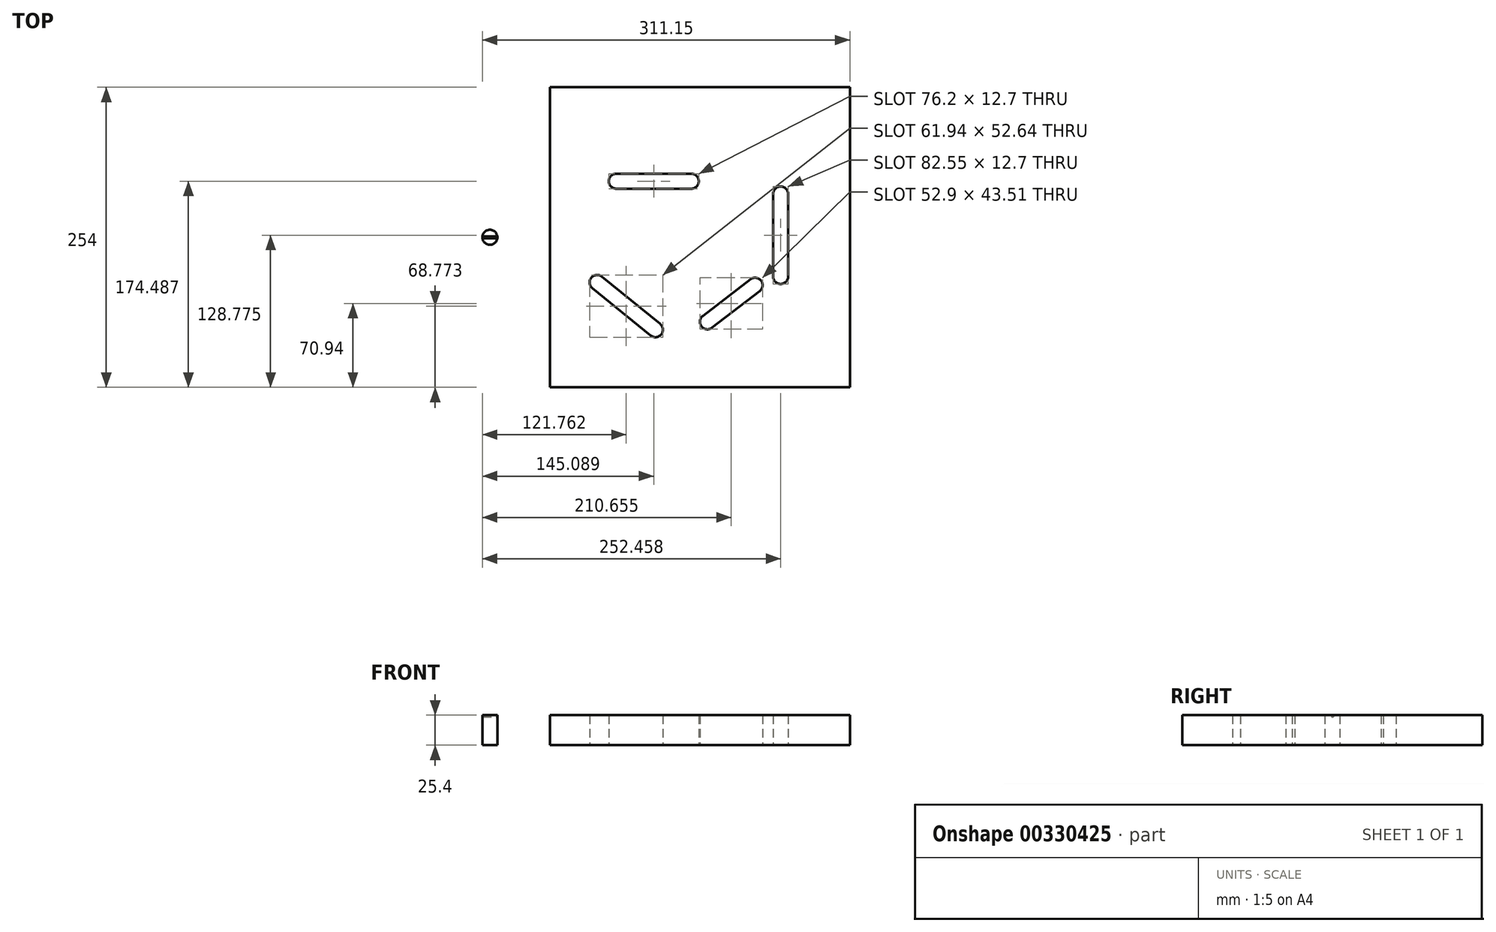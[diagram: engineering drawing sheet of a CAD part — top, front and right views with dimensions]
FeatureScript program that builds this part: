
annotation { "Feature Type Name" : "Feature", "Feature Type Description" : "" }
export const myFeature = defineFeature(function(context is Context, id is Id, definition is map)
    precondition{}
    {
        {
            var Q0;
            Q0=qCreatedBy(makeId("Top.planeOp"),FACE);
            var sketch = newSketch(context, id + "F0", { "sketchPlane" : qUnion([Q0])});
            skLineSegment(sketch, "E0.bottom", {"start": v(127, -127) * mm, "end": v(-127, -127) * mm});
            skLineSegment(sketch, "E0.top", {"start": v(127, 127) * mm, "end": v(-127, 127) * mm});
            skLineSegment(sketch, "E0.left", {"start": v(127, -127) * mm, "end": v(127, 127) * mm});
            skLineSegment(sketch, "E0.right", {"start": v(-127, -127) * mm, "end": v(-127, 127) * mm});
            skPoint(sketch, "E0.middle", {"position": v(0, 0) * mm});
            skLineSegment(sketch, "E1", {"start": v(-87.04, -38.22) * mm, "end": v(-37.73, -78.23) * mm});
            skLineSegment(sketch, "E2", {"start": v(68.3, 36.7) * mm, "end": v(68.3, -33.15) * mm});
            skLineSegment(sketch, "E3", {"start": v(-70.81, 47.49) * mm, "end": v(-7.31, 47.49) * mm});
            skArc(sketch, "E4.0.startCap", {"start": v(-70.81, 41.14) * mm, "mid": v(-77.16, 47.49) * mm, "end": v(-70.81, 53.84) * mm});
            skArc(sketch, "E4.0.endCap", {"start": v(-7.31, 53.84) * mm, "mid": v(-0.96, 47.49) * mm, "end": v(-7.31, 41.14) * mm});
            skLineSegment(sketch, "E4.0.left", {"start": v(-70.81, 53.84) * mm, "end": v(-7.31, 53.84) * mm});
            skLineSegment(sketch, "E4.0.right", {"start": v(-70.81, 41.14) * mm, "end": v(-7.31, 41.14) * mm});
            skArc(sketch, "E4.1.startCap", {"start": v(-91.05, -43.16) * mm, "mid": v(-91.98, -34.22) * mm, "end": v(-83.04, -33.3) * mm});
            skArc(sketch, "E4.1.endCap", {"start": v(-33.73, -73.3) * mm, "mid": v(-32.8, -82.23) * mm, "end": v(-41.73, -83.16) * mm});
            skLineSegment(sketch, "E4.1.left", {"start": v(-83.04, -33.3) * mm, "end": v(-33.73, -73.3) * mm});
            skLineSegment(sketch, "E4.1.right", {"start": v(-91.05, -43.16) * mm, "end": v(-41.73, -83.16) * mm});
            skArc(sketch, "E4.2.startCap", {"start": v(61.96, 36.7) * mm, "mid": v(68.3, 43.05) * mm, "end": v(74.66, 36.7) * mm});
            skArc(sketch, "E4.2.endCap", {"start": v(74.66, -33.15) * mm, "mid": v(68.3, -39.5) * mm, "end": v(61.96, -33.15) * mm});
            skLineSegment(sketch, "E4.2.left", {"start": v(74.66, 36.7) * mm, "end": v(74.66, -33.15) * mm});
            skLineSegment(sketch, "E4.2.right", {"start": v(61.96, 36.7) * mm, "end": v(61.96, -33.15) * mm});
            skCircle(sketch, "E5", {"center": v(-177.8, 0) * mm, "radius": 6.35 * mm});
            skLineSegment(sketch, "E6", {"start": v(6.35, -71.52) * mm, "end": v(46.66, -40.6) * mm});
            skArc(sketch, "E7.0.startCap", {"start": v(10.21, -76.56) * mm, "mid": v(1.31, -75.38) * mm, "end": v(2.49, -66.48) * mm});
            skArc(sketch, "E7.0.endCap", {"start": v(42.8, -35.56) * mm, "mid": v(51.7, -36.74) * mm, "end": v(50.52, -45.64) * mm});
            skLineSegment(sketch, "E7.0.left", {"start": v(2.49, -66.48) * mm, "end": v(42.8, -35.56) * mm});
            skLineSegment(sketch, "E7.0.right", {"start": v(10.21, -76.56) * mm, "end": v(50.52, -45.64) * mm});
            skSolve(sketch);
        }
        {
            var Q0;
            Q0=makeQuery(id+"F0.imprint","IMPRINT",FACE,{"disambiguationData":[TD([[makeQuery(id+"F0.imprint","IMPRINT",EDGE,{"derivedFrom":sQuery(id+"F0.wireOp",EDGE,"E0.bottom")}),-1.0]])]});
            var Q1;
            Q1=makeQuery(id+"F0.imprint","IMPRINT",FACE,{"disambiguationData":[TD([[makeQuery(id+"F0.imprint","IMPRINT",EDGE,{"derivedFrom":sQuery(id+"F0.wireOp",EDGE,"E5")}),1.0]])]});
            extrude(context, id + "F1", {"entities" : qUnion([Q0, Q1]), "depth" : 25.4 * mm});
        }
        {
            var Q0;
            Q0=makeQuery(id+"F1.opExtrude","CAP_FACE",FACE,{"disambiguationData":[OSD([sQuery(id+"F0.wireOp",EDGE,"E5")])],"isStart":false});
            var sketch = newSketch(context, id + "F2", { "sketchPlane" : qUnion([Q0])});
            skLineSegment(sketch, "E8.bottom", {"start": v(-185.42, 0.76) * mm, "end": v(-170.18, 0.76) * mm});
            skLineSegment(sketch, "E8.top", {"start": v(-185.42, -0.76) * mm, "end": v(-170.18, -0.76) * mm});
            skLineSegment(sketch, "E8.left", {"start": v(-185.42, 0.76) * mm, "end": v(-185.42, -0.76) * mm});
            skLineSegment(sketch, "E8.right", {"start": v(-170.18, 0.76) * mm, "end": v(-170.18, -0.76) * mm});
            skPoint(sketch, "E8.middle", {"position": v(-177.8, 0) * mm});
            skSolve(sketch);
        }
        {
            var Q0;
            Q0 = qSketchRegion(id + "F2", true);
            extrude(context, id + "F3", {"entities" : qUnion([Q0]), "operationType" : NewBodyOperationType.REMOVE, "oppositeDirection" : true, "depth" : 1.52 * mm});
        }
    });
